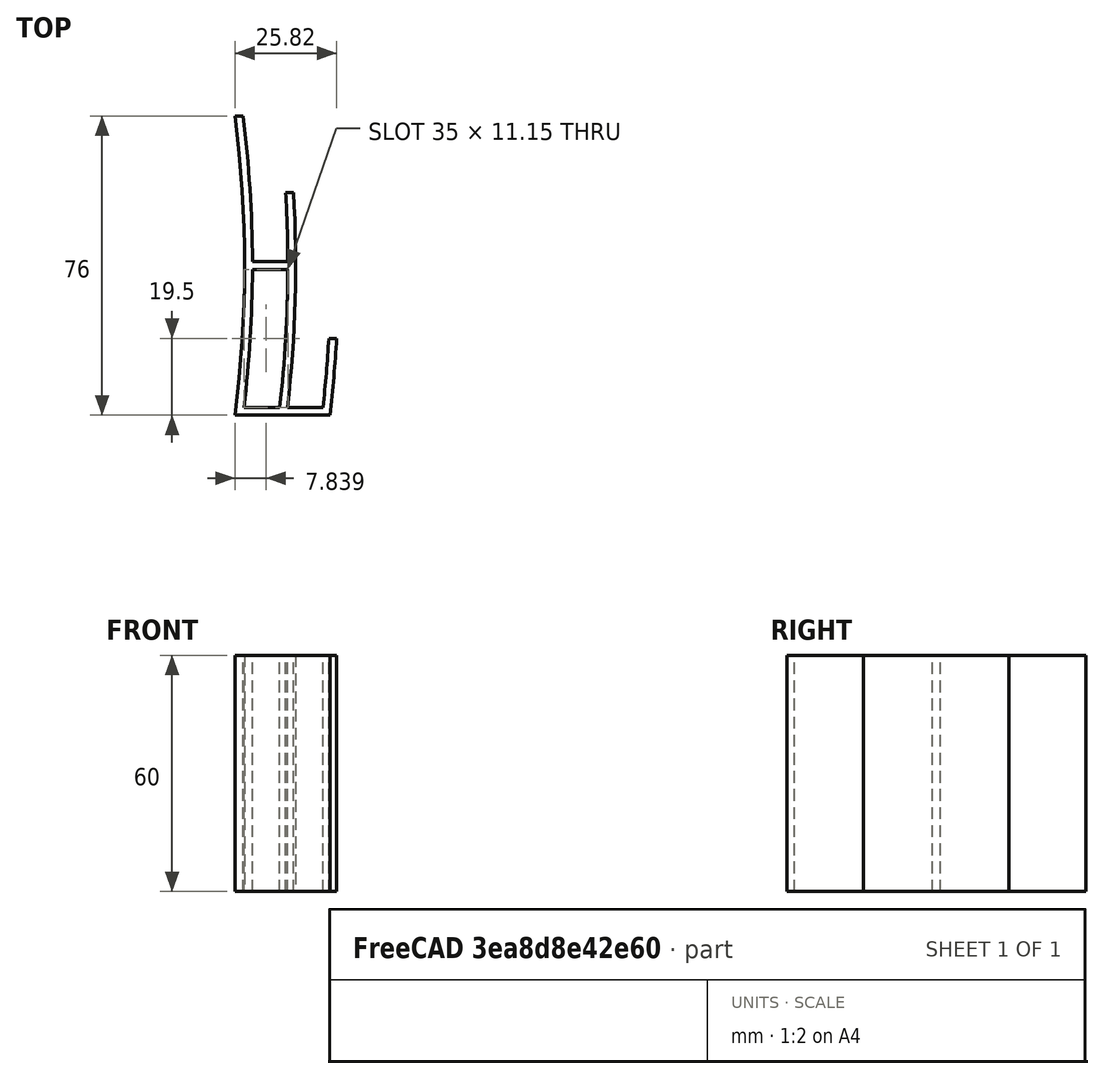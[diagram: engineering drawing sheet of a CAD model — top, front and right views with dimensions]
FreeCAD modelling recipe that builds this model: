
FCSTD DOCUMENT  (FreeCAD 0.20R29177 (Git))
Label: Continuity Camera Mount
License: All rights reserved
LicenseURL: http://en.wikipedia.org/wiki/All_rights_reserved
objects: Sketcher::SketchObject×1, Spreadsheet::Sheet×1, PartDesign::Pad×1, PartDesign::Body×1, App::Part×1
note: 4 computed .brp shape members not serialized (recipe doc carries the construction recipe); baked Part::Feature solids carry a one-line shape summary decoded from their .brp

FEATURE [Sketcher::SketchObject] Sketch
  FullyConstrained = true
  MapMode = 5
  Support = -> [XY_Plane001]
  expr: Constraints[10] = Spreadsheet.wall_thickness
  expr: Constraints[11] = Spreadsheet.wall_thickness
  expr: Constraints[12] = Spreadsheet.wall_thickness
  expr: Constraints[13] = Spreadsheet.wall_thickness
  expr: Constraints[15] = Spreadsheet.wall_thickness
  expr: Constraints[16] = Spreadsheet.phone_thickness
  expr: Constraints[17] = Spreadsheet.phone_thickness
  expr: Constraints[18] = Spreadsheet.step_difference - Spreadsheet.wall_thickness
  expr: Constraints[19] = Spreadsheet.camera_side_wall_height
  expr: Constraints[20] = Spreadsheet.display_side_wall_height
  expr: Constraints[21] = Spreadsheet.display_side_wall_height
  expr: Constraints[24] = Spreadsheet.curve_radius
  expr: Constraints[25] = Spreadsheet.wall_thickness
  expr: Constraints[29] = Spreadsheet.curve_radius + Spreadsheet.wall_thickness
  expr: Constraints[33] = Spreadsheet.curve_radius + Spreadsheet.wall_thickness
  sketch-geometry (16):
    g0: LineSegment StartX=2.41474 StartY=-35 StartZ=0 EndX=11.4147 EndY=-35 EndZ=0
    g1: LineSegment StartX=10.8656 StartY=-17.5 StartZ=0 EndX=12.8656 EndY=-17.5 EndZ=0
    g2: LineSegment StartX=-2 StartY=2 StartZ=0 EndX=0.0161313 EndY=2 EndZ=0
    g3: LineSegment StartX=11.3356 StartY=-72 StartZ=0 EndX=20.3356 EndY=-72 EndZ=0
    g4: LineSegment StartX=21.8228 StartY=-54.5 StartZ=0 EndX=23.8228 EndY=-54.5 EndZ=0
    g5: LineSegment StartX=22.1149 StartY=-74 StartZ=0 EndX=-2 EndY=-74 EndZ=0
    g6: LineSegment StartX=2.41474 StartY=-37 StartZ=0 EndX=11.4147 EndY=-37 EndZ=0
    g7: LineSegment StartX=9.32572 StartY=-72 StartZ=0 EndX=0.263026 EndY=-72 EndZ=0
    g8: ArcOfCircle CenterX=-299.584 CenterY=-36 CenterZ=0 NormalX=0 NormalY=0 NormalZ=1 AngleXU=0 Radius=300 StartAngle=6.15618 EndAngle=6.41019
    g9: ArcOfCircle CenterX=-299.584 CenterY=-36 CenterZ=0 NormalX=0 NormalY=0 NormalZ=1 AngleXU=0 Radius=302 StartAngle=0.00331126 EndAngle=0.126162
    g10: ArcOfCircle CenterX=-299.584 CenterY=-36 CenterZ=0 NormalX=0 NormalY=0 NormalZ=1 AngleXU=0 Radius=302 StartAngle=6.1637 EndAngle=6.27987
    g11: ArcOfCircle CenterX=-299.584 CenterY=-36 CenterZ=0 NormalX=0 NormalY=0 NormalZ=1 AngleXU=0 Radius=312.996 StartAngle=6.16791 EndAngle=6.34233
    g12: ArcOfCircle CenterX=-299.584 CenterY=-36 CenterZ=0 NormalX=0 NormalY=0 NormalZ=1 AngleXU=0 Radius=311 StartAngle=0.00321544 EndAngle=0.0595207
    g13: ArcOfCircle CenterX=-299.584 CenterY=-36 CenterZ=0 NormalX=0 NormalY=0 NormalZ=1 AngleXU=0 Radius=311 StartAngle=6.16717 EndAngle=6.27997
    g14: ArcOfCircle CenterX=-299.584 CenterY=-36 CenterZ=0 NormalX=0 NormalY=0 NormalZ=1 AngleXU=0 Radius=321.938 StartAngle=6.17113 EndAngle=6.22569
    g15: ArcOfCircle CenterX=-299.584 CenterY=-36 CenterZ=0 NormalX=0 NormalY=0 NormalZ=1 AngleXU=0 Radius=323.935 StartAngle=6.16561 EndAngle=6.22604
  constraints (49):
    c: Horizontal(g0)
    c: Horizontal(g1)
    c: Horizontal(g2)
    c: Horizontal(g3)
    c: Horizontal(g4)
    c: Horizontal(g5)
    c: Horizontal(g7)
    c: Horizontal(g6)
    c: Vertical(g0,g6)
    c: Vertical(g0,g6)
    c: DistanceX(g2,g-1) = 2
    c: DistanceX(g1,g1) = 2
    c: DistanceX(g4,g4) = 2
    c: DistanceY(g6,g0) = 2
    c: Horizontal(g3,g7)
    c: DistanceY(g5,g7) = 2
    c: DistanceX(g0,g0) = 9
    c: DistanceX(g3,g3) = 9
    c: DistanceY(g7,g6) = 35
    c: DistanceY(g0,g-1) = 35
    c: DistanceY(g0,g1) = 17.5
    c: DistanceY(g3,g4) = 17.5
    c: Coincident(g8,g2)
    c: Coincident(g8,g5)
    c: Radius(g8) = 300
    c: DistanceX(g5,g-1) = 2
    c: Coincident(g9,g8)
    c: Coincident(g9,g2)
    c: Coincident(g9,g0)
    c: Radius(g9) = 302
    c: Coincident(g10,g8)
    c: Coincident(g10,g6)
    c: Coincident(g10,g7)
    c: Radius(g10) = 302
    c: Coincident(g11,g8)
    c: Coincident(g11,g1)
    c: Coincident(g11,g3)
    c: Coincident(g12,g8)
    c: Coincident(g12,g1)
    c: Coincident(g12,g0)
    c: Coincident(g13,g8)
    c: Coincident(g13,g6)
    c: Coincident(g13,g7)
    c: Coincident(g14,g8)
    c: Coincident(g14,g4)
    c: Coincident(g14,g3)
    c: Coincident(g15,g8)
    c: Coincident(g15,g4)
    c: Coincident(g15,g5)
FEATURE [Spreadsheet::Sheet] Spreadsheet
  cells = A1=wall_thickness; B1(wall_thickness)=2; A2=phone_thickness; B2(phone_thickness)=9; A3=step_difference; B3(step_difference)=37; A4=camera_side_wall_height; B4(camera_side_wall_height)=35; A5=display_side_wall_height; B5(display_side_wall_height)=17.5; A6=width; B6(width)=60; A7=curve_radius; B7(curve_radius)=300
FEATURE [PartDesign::Pad] Pad
  Direction = (0,0,1)
  Length = 60
  Length2 = 10
  Profile = -> Sketch
  ReferenceAxis = -> Sketch [N_Axis]
  Type = 0
  expr: Length = Spreadsheet.width
FEATURE [PartDesign::Body] Body
  Group = -> [Sketch,Pad]
  Origin = -> Origin001
  Tip = -> Pad
FEATURE [App::Part] Part
  Group = -> [Body]
  Origin = -> Origin
